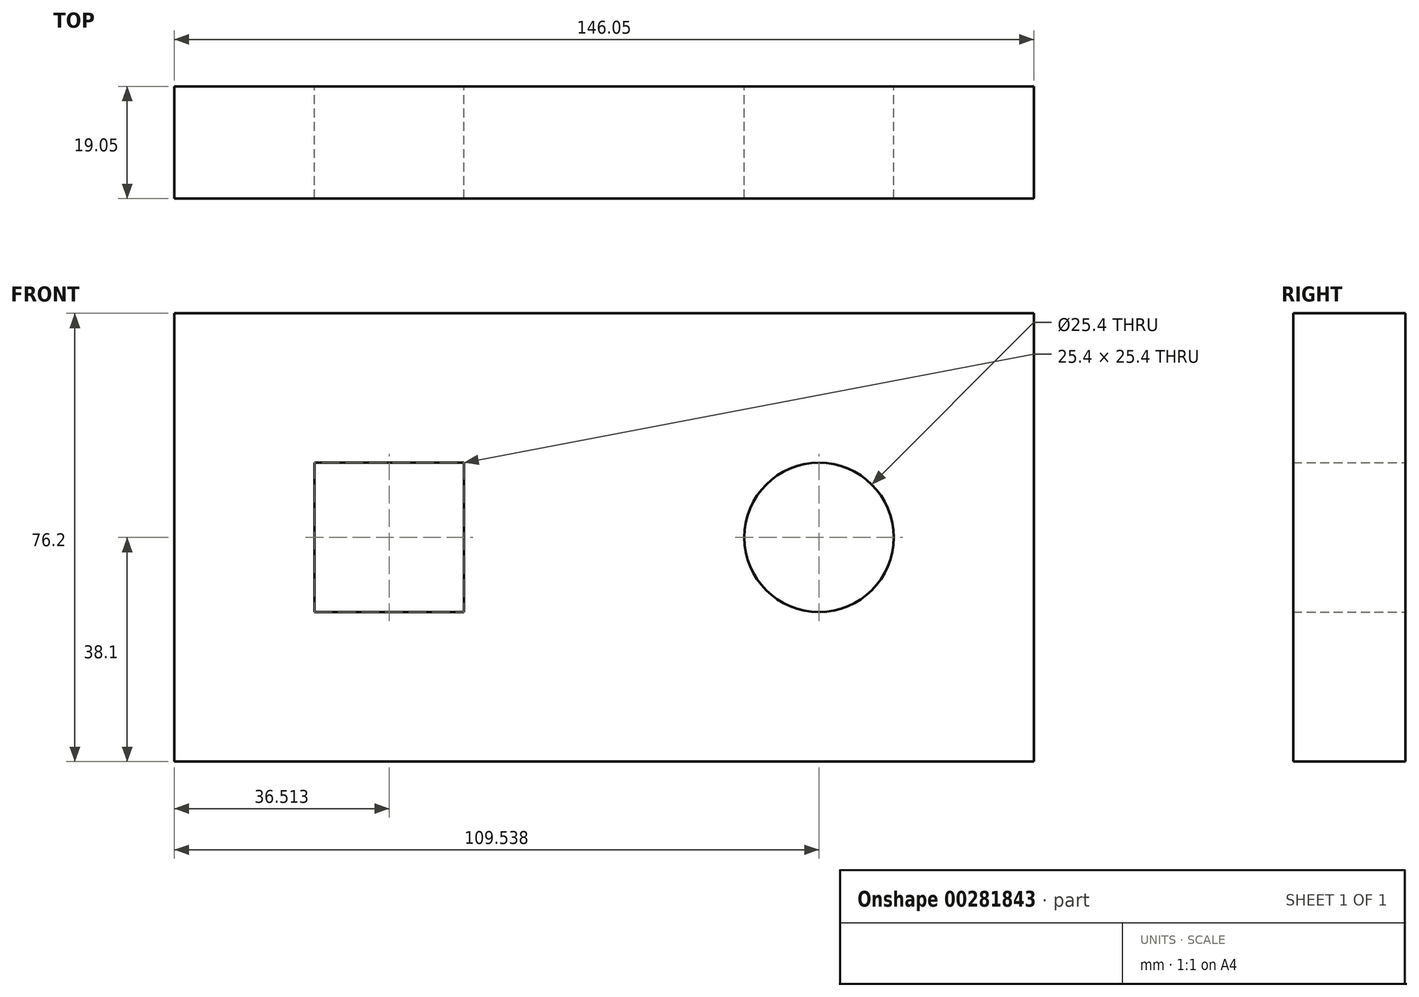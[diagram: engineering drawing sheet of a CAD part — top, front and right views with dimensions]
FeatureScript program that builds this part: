
annotation { "Feature Type Name" : "Feature", "Feature Type Description" : "" }
export const myFeature = defineFeature(function(context is Context, id is Id, definition is map)
    precondition{}
    {
        {
            var Q0;
            Q0=qCreatedBy(makeId("Front.planeOp"),FACE);
            var sketch = newSketch(context, id + "F0", { "sketchPlane" : qUnion([Q0])});
            skLineSegment(sketch, "E0.bottom", {"start": v(0, 0) * mm, "end": v(-146.05, 0) * mm});
            skLineSegment(sketch, "E0.top", {"start": v(0, 76.2) * mm, "end": v(-146.05, 76.2) * mm});
            skLineSegment(sketch, "E0.left", {"start": v(0, 0) * mm, "end": v(0, 76.2) * mm});
            skLineSegment(sketch, "E0.right", {"start": v(-146.05, 0) * mm, "end": v(-146.05, 76.2) * mm});
            skLineSegment(sketch, "E1.bottom", {"start": v(-96.84, 25.4) * mm, "end": v(-122.24, 25.4) * mm});
            skLineSegment(sketch, "E1.top", {"start": v(-96.84, 50.8) * mm, "end": v(-122.24, 50.8) * mm});
            skLineSegment(sketch, "E1.left", {"start": v(-96.84, 25.4) * mm, "end": v(-96.84, 50.8) * mm});
            skLineSegment(sketch, "E1.right", {"start": v(-122.24, 25.4) * mm, "end": v(-122.24, 50.8) * mm});
            skCircle(sketch, "E2", {"center": v(-36.51, 38.1) * mm, "radius": 12.7 * mm});
            skSolve(sketch);
        }
        {
            var Q0;
            Q0 = qSketchRegion(id + "F0", true);
            extrude(context, id + "F1", {"entities" : qUnion([Q0]), "depth" : 19.05 * mm});
        }
    });
